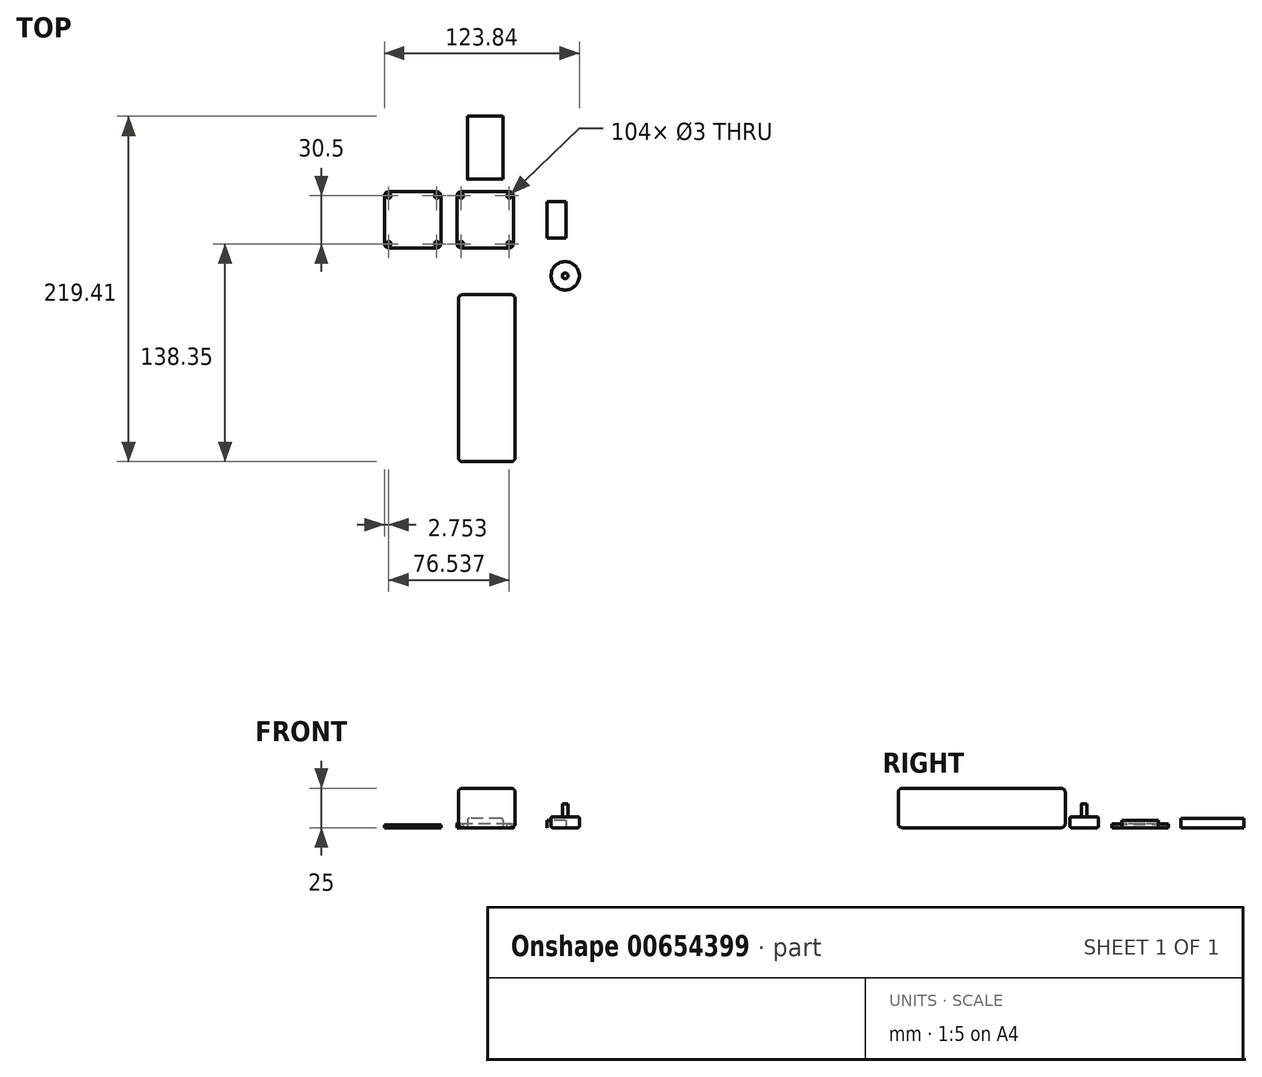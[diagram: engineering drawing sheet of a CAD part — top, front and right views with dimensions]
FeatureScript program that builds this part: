
annotation { "Feature Type Name" : "Feature", "Feature Type Description" : "" }
export const myFeature = defineFeature(function(context is Context, id is Id, definition is map)
    precondition{}
    {
        {
            var Q0;
            Q0=qCreatedBy(makeId("Top.planeOp"),FACE);
            var sketch = newSketch(context, id + "F0", { "sketchPlane" : qUnion([Q0])});
            skLineSegment(sketch, "E0.bottom", {"start": v(18, 18) * mm, "end": v(-18, 18) * mm});
            skLineSegment(sketch, "E0.top", {"start": v(18, -18) * mm, "end": v(-18, -18) * mm});
            skLineSegment(sketch, "E0.left", {"start": v(18, 18) * mm, "end": v(18, -18) * mm});
            skLineSegment(sketch, "E0.right", {"start": v(-18, 18) * mm, "end": v(-18, -18) * mm});
            skPoint(sketch, "E0.middle", {"position": v(0, 0) * mm});
            skSolve(sketch);
        }
        {
            var Q0;
            Q0=qSketchRegion(id+"F0",true);
            extrude(context, id + "F1", {"entities" : qUnion([Q0]), "depth" : 2.54 * mm, "offsetDistance" : 25.4 * mm});
        }
        {
            var Q0;
            Q0=makeQuery(id+"F1.opExtrude","SWEPT_EDGE",EDGE,{"disambiguationData":[OSD([sQuery(id+"F0.wireOp",EDGE,"E0.bottom"),sQuery(id+"F0.wireOp",EDGE,"E0.right")])]});
            var Q1;
            Q1=makeQuery(id+"F1.opExtrude","SWEPT_EDGE",EDGE,{"disambiguationData":[OSD([sQuery(id+"F0.wireOp",EDGE,"E0.bottom"),sQuery(id+"F0.wireOp",EDGE,"E0.left")])]});
            var Q2;
            Q2=makeQuery(id+"F1.opExtrude","SWEPT_EDGE",EDGE,{"disambiguationData":[OSD([sQuery(id+"F0.wireOp",EDGE,"E0.top"),sQuery(id+"F0.wireOp",EDGE,"E0.left")])]});
            var Q3;
            Q3=makeQuery(id+"F1.opExtrude","SWEPT_EDGE",EDGE,{"disambiguationData":[OSD([sQuery(id+"F0.wireOp",EDGE,"E0.top"),sQuery(id+"F0.wireOp",EDGE,"E0.right")])]});
            fillet(context, id + "F2", {"entities" : qUnion([Q0, Q1, Q2, Q3]), "radius" : 3.17 * mm, "tangentPropagation" : true, "allowEdgeOverflow" : false});
        }
        {
            var Q0;
            Q0=makeQuery(id+"F1.opExtrude","CAP_FACE",FACE,{"disambiguationData":[OSD([sQuery(id+"F0.wireOp",EDGE,"E0.bottom"),sQuery(id+"F0.wireOp",EDGE,"E0.top"),sQuery(id+"F0.wireOp",EDGE,"E0.left"),sQuery(id+"F0.wireOp",EDGE,"E0.right")])],"isStart":false});
            var sketch = newSketch(context, id + "F3", { "sketchPlane" : qUnion([Q0])});
            skLineSegment(sketch, "E1.bottom", {"start": v(15.25, 15.25) * mm, "end": v(-15.25, 15.25) * mm, "construction": true});
            skLineSegment(sketch, "E1.top", {"start": v(15.25, -15.25) * mm, "end": v(-15.25, -15.25) * mm, "construction": true});
            skLineSegment(sketch, "E1.left", {"start": v(15.25, 15.25) * mm, "end": v(15.25, -15.25) * mm, "construction": true});
            skLineSegment(sketch, "E1.right", {"start": v(-15.25, 15.25) * mm, "end": v(-15.25, -15.25) * mm, "construction": true});
            skPoint(sketch, "E1.middle", {"position": v(0, 0) * mm});
            skCircle(sketch, "E2", {"center": v(-15.25, 15.25) * mm, "radius": 1.5 * mm});
            skLineSegment(sketch, "E3", {"start": v(-18, 0) * mm, "end": v(18, 0) * mm, "construction": true});
            skLineSegment(sketch, "E4", {"start": v(0, 18) * mm, "end": v(0, -18) * mm, "construction": true});
            skCircle(sketch, "E5.MirrorC", {"center": v(15.25, 15.25) * mm, "radius": 1.5 * mm});
            skCircle(sketch, "E6.MirrorC", {"center": v(-15.25, -15.25) * mm, "radius": 1.5 * mm});
            skCircle(sketch, "E7.MirrorC", {"center": v(15.25, -15.25) * mm, "radius": 1.5 * mm});
            skSolve(sketch);
        }
        {
            var Q0;
            Q0=qSketchRegion(id+"F3",true);
            extrude(context, id + "F4", {"entities" : qUnion([Q0]), "operationType" : NewBodyOperationType.REMOVE, "oppositeDirection" : true, "depth" : 2.54 * mm, "offsetDistance" : 25.4 * mm});
        }
        {
            var Q0;
            Q0=qCreatedBy(makeId("Top.planeOp"),FACE);
            var sketch = newSketch(context, id + "F5", { "sketchPlane" : qUnion([Q0])});
            skLineSegment(sketch, "E8.bottom", {"start": v(51.23, 11.5) * mm, "end": v(39.23, 11.5) * mm});
            skLineSegment(sketch, "E8.top", {"start": v(51.23, -11.5) * mm, "end": v(39.23, -11.5) * mm});
            skLineSegment(sketch, "E8.left", {"start": v(51.23, 11.5) * mm, "end": v(51.23, -11.5) * mm});
            skLineSegment(sketch, "E8.right", {"start": v(39.23, 11.5) * mm, "end": v(39.23, -11.5) * mm});
            skPoint(sketch, "E8.middle", {"position": v(45.23, 0) * mm});
            skSolve(sketch);
        }
        {
            var Q0;
            Q0=qSketchRegion(id+"F5",true);
            extrude(context, id + "F6", {"entities" : qUnion([Q0]), "depth" : 4.5 * mm, "offsetDistance" : 25.4 * mm});
        }
        {
            var Q0;
            Q0=qCreatedBy(makeId("Top.planeOp"),FACE);
            var sketch = newSketch(context, id + "F7", { "sketchPlane" : qUnion([Q0])});
            skLineSegment(sketch, "E9.bottom", {"start": v(-28.04, 18) * mm, "end": v(-64.04, 18) * mm});
            skLineSegment(sketch, "E9.top", {"start": v(-28.04, -18) * mm, "end": v(-64.04, -18) * mm});
            skLineSegment(sketch, "E9.left", {"start": v(-28.04, 18) * mm, "end": v(-28.04, -18) * mm});
            skLineSegment(sketch, "E9.right", {"start": v(-64.04, 18) * mm, "end": v(-64.04, -18) * mm});
            skPoint(sketch, "E9.middle", {"position": v(-46.04, 0) * mm});
            skSolve(sketch);
        }
        {
            var Q0;
            Q0=qSketchRegion(id+"F7",true);
            extrude(context, id + "F8", {"entities" : qUnion([Q0]), "depth" : 1.75 * mm, "offsetDistance" : 25.4 * mm});
        }
        {
            var Q0;
            Q0=makeQuery(id+"F8.opExtrude","CAP_FACE",FACE,{"disambiguationData":[OSD([sQuery(id+"F7.wireOp",EDGE,"E9.bottom"),sQuery(id+"F7.wireOp",EDGE,"E9.top"),sQuery(id+"F7.wireOp",EDGE,"E9.left"),sQuery(id+"F7.wireOp",EDGE,"E9.right")])],"isStart":false});
            var sketch = newSketch(context, id + "F9", { "sketchPlane" : qUnion([Q0])});
            skLineSegment(sketch, "E10", {"start": v(-46.04, 18) * mm, "end": v(-46.04, -18) * mm, "construction": true});
            skLineSegment(sketch, "E11", {"start": v(-64.04, 0) * mm, "end": v(-28.04, 0) * mm, "construction": true});
            skLineSegment(sketch, "E12.bottom", {"start": v(-30.79, 15.25) * mm, "end": v(-61.29, 15.25) * mm, "construction": true});
            skLineSegment(sketch, "E12.top", {"start": v(-30.79, -15.25) * mm, "end": v(-61.29, -15.25) * mm, "construction": true});
            skLineSegment(sketch, "E12.left", {"start": v(-30.79, 15.25) * mm, "end": v(-30.79, -15.25) * mm, "construction": true});
            skLineSegment(sketch, "E12.right", {"start": v(-61.29, 15.25) * mm, "end": v(-61.29, -15.25) * mm, "construction": true});
            skPoint(sketch, "E12.middle", {"position": v(-46.04, 0) * mm});
            skCircle(sketch, "E13", {"center": v(-61.29, 15.25) * mm, "radius": 1.5 * mm});
            skCircle(sketch, "E14.MirrorC", {"center": v(-30.79, 15.25) * mm, "radius": 1.5 * mm});
            skCircle(sketch, "E15.MirrorC", {"center": v(-61.29, -15.25) * mm, "radius": 1.5 * mm});
            skCircle(sketch, "E16.MirrorC", {"center": v(-30.79, -15.25) * mm, "radius": 1.5 * mm});
            skSolve(sketch);
        }
        {
            var Q0;
            Q0=qSketchRegion(id+"F9",true);
            extrude(context, id + "F10", {"entities" : qUnion([Q0]), "operationType" : NewBodyOperationType.REMOVE, "oppositeDirection" : true, "depth" : 1.75 * mm, "offsetDistance" : 25.4 * mm});
        }
        {
            var Q0;
            Q0=makeQuery(id+"F8.opExtrude","SWEPT_EDGE",EDGE,{"disambiguationData":[OSD([sQuery(id+"F7.wireOp",EDGE,"E9.bottom"),sQuery(id+"F7.wireOp",EDGE,"E9.right")])]});
            var Q1;
            Q1=makeQuery(id+"F8.opExtrude","SWEPT_EDGE",EDGE,{"disambiguationData":[OSD([sQuery(id+"F7.wireOp",EDGE,"E9.bottom"),sQuery(id+"F7.wireOp",EDGE,"E9.left")])]});
            var Q2;
            Q2=makeQuery(id+"F8.opExtrude","SWEPT_EDGE",EDGE,{"disambiguationData":[OSD([sQuery(id+"F7.wireOp",EDGE,"E9.top"),sQuery(id+"F7.wireOp",EDGE,"E9.left")])]});
            var Q3;
            Q3=makeQuery(id+"F8.opExtrude","SWEPT_EDGE",EDGE,{"disambiguationData":[OSD([sQuery(id+"F7.wireOp",EDGE,"E9.top"),sQuery(id+"F7.wireOp",EDGE,"E9.right")])]});
            fillet(context, id + "F11", {"entities" : qUnion([Q0, Q1, Q2, Q3]), "radius" : 3.17 * mm, "tangentPropagation" : true, "allowEdgeOverflow" : false});
        }
        {
            var Q0;
            Q0=qCreatedBy(makeId("Top.planeOp"),FACE);
            var sketch = newSketch(context, id + "F12", { "sketchPlane" : qUnion([Q0])});
            skLineSegment(sketch, "E17.bottom", {"start": v(11.25, 65.81) * mm, "end": v(11.25, 25.81) * mm});
            skLineSegment(sketch, "E17.top", {"start": v(-11.25, 65.81) * mm, "end": v(-11.25, 25.81) * mm});
            skLineSegment(sketch, "E17.left", {"start": v(11.25, 65.81) * mm, "end": v(-11.25, 65.81) * mm});
            skLineSegment(sketch, "E17.right", {"start": v(11.25, 25.81) * mm, "end": v(-11.25, 25.81) * mm});
            skPoint(sketch, "E17.middle", {"position": v(0, 45.81) * mm});
            skSolve(sketch);
        }
        {
            var Q0;
            Q0=qSketchRegion(id+"F12",true);
            extrude(context, id + "F13", {"entities" : qUnion([Q0]), "depth" : 6 * mm, "offsetDistance" : 25.4 * mm});
        }
        {
            var Q0;
            Q0=makeQuery(id+"F13.opExtrude","CAP_EDGE",EDGE,{"disambiguationData":[OSD([sQuery(id+"F12.wireOp",EDGE,"E17.bottom")])],"isStart":false});
            var Q1;
            Q1=makeQuery(id+"F13.opExtrude","CAP_EDGE",EDGE,{"disambiguationData":[OSD([sQuery(id+"F12.wireOp",EDGE,"E17.bottom")])],"isStart":true});
            var Q2;
            Q2=makeQuery(id+"F13.opExtrude","CAP_EDGE",EDGE,{"disambiguationData":[OSD([sQuery(id+"F12.wireOp",EDGE,"E17.top")])],"isStart":true});
            var Q3;
            Q3=makeQuery(id+"F13.opExtrude","CAP_EDGE",EDGE,{"disambiguationData":[OSD([sQuery(id+"F12.wireOp",EDGE,"E17.top")])],"isStart":false});
            fillet(context, id + "F14", {"entities" : qUnion([Q0, Q1, Q2, Q3]), "radius" : 1.27 * mm, "tangentPropagation" : true, "allowEdgeOverflow" : false});
        }
        {
            var Q0;
            Q0=qCreatedBy(makeId("Top.planeOp"),FACE);
            var sketch = newSketch(context, id + "F15", { "sketchPlane" : qUnion([Q0])});
            skLineSegment(sketch, "E18.bottom", {"start": v(-17, -47.6) * mm, "end": v(-17, -153.6) * mm});
            skLineSegment(sketch, "E18.top", {"start": v(19, -47.6) * mm, "end": v(19, -153.6) * mm});
            skLineSegment(sketch, "E18.left", {"start": v(-17, -47.6) * mm, "end": v(19, -47.6) * mm});
            skLineSegment(sketch, "E18.right", {"start": v(-17, -153.6) * mm, "end": v(19, -153.6) * mm});
            skPoint(sketch, "E18.middle", {"position": v(1, -100.6) * mm});
            skLineSegment(sketch, "E19", {"start": v(0, 0) * mm, "end": v(0, -101.6) * mm, "construction": true});
            skSolve(sketch);
        }
        {
            var Q0;
            Q0=qSketchRegion(id+"F15",true);
            extrude(context, id + "F16", {"entities" : qUnion([Q0]), "depth" : 25 * mm, "offsetDistance" : 25.4 * mm});
        }
        {
            var Q0;
            Q0=makeQuery(id+"F16.opExtrude","CAP_FACE",FACE,{"disambiguationData":[OSD([sQuery(id+"F15.wireOp",EDGE,"E18.bottom"),sQuery(id+"F15.wireOp",EDGE,"E18.top"),sQuery(id+"F15.wireOp",EDGE,"E18.left"),sQuery(id+"F15.wireOp",EDGE,"E18.right")])],"isStart":false});
            var Q1;
            Q1=makeQuery(id+"F16.opExtrude","SWEPT_FACE",FACE,{"disambiguationData":[OSD([sQuery(id+"F15.wireOp",EDGE,"E18.right")])]});
            var Q2;
            Q2=makeQuery(id+"F16.opExtrude","CAP_FACE",FACE,{"disambiguationData":[OSD([sQuery(id+"F15.wireOp",EDGE,"E18.bottom"),sQuery(id+"F15.wireOp",EDGE,"E18.top"),sQuery(id+"F15.wireOp",EDGE,"E18.left"),sQuery(id+"F15.wireOp",EDGE,"E18.right")])],"isStart":true});
            var Q3;
            Q3=makeQuery(id+"F16.opExtrude","SWEPT_FACE",FACE,{"disambiguationData":[OSD([sQuery(id+"F15.wireOp",EDGE,"E18.left")])]});
            fillet(context, id + "F17", {"entities" : qUnion([Q0, Q1, Q2, Q3]), "radius" : 2.54 * mm, "tangentPropagation" : true, "allowEdgeOverflow" : false});
        }
        {
            var Q0;
            Q0=qCreatedBy(makeId("Top.planeOp"),FACE);
            var sketch = newSketch(context, id + "F18", { "sketchPlane" : qUnion([Q0])});
            skLineSegment(sketch, "E20", {"start": v(0, 0) * mm, "end": v(0, -35.56) * mm, "construction": true});
            skLineSegment(sketch, "E21", {"start": v(0, -35.56) * mm, "end": v(50.8, -35.56) * mm, "construction": true});
            skCircle(sketch, "E22", {"center": v(50.8, -35.56) * mm, "radius": 9 * mm});
            skSolve(sketch);
        }
        {
            var Q0;
            Q0=qSketchRegion(id+"F18",true);
            extrude(context, id + "F19", {"entities" : qUnion([Q0]), "depth" : 7 * mm, "offsetDistance" : 25.4 * mm});
        }
        {
            var Q0;
            Q0=makeQuery(id+"F19.opExtrude","CAP_FACE",FACE,{"disambiguationData":[OSD([sQuery(id+"F18.wireOp",EDGE,"E22")])],"isStart":false});
            var sketch = newSketch(context, id + "F20", { "sketchPlane" : qUnion([Q0])});
            skCircle(sketch, "E23", {"center": v(50.8, -35.56) * mm, "radius": 1.84 * mm});
            skSolve(sketch);
        }
        {
            var Q0;
            Q0=qSketchRegion(id+"F20",true);
            extrude(context, id + "F21", {"entities" : qUnion([Q0]), "operationType" : NewBodyOperationType.ADD, "depth" : 8 * mm, "offsetDistance" : 25.4 * mm});
        }
        {
            var Q0;
            Q0=makeQuery(id+"F19.opExtrude","CAP_FACE",FACE,{"disambiguationData":[OSD([sQuery(id+"F18.wireOp",EDGE,"E22")])],"isStart":true});
            var Q1;
            Q1=makeQuery(id+"F19.opExtrude","CAP_FACE",FACE,{"disambiguationData":[OSD([sQuery(id+"F18.wireOp",EDGE,"E22")])],"isStart":false});
            fillet(context, id + "F22", {"entities" : qUnion([Q0, Q1]), "radius" : 1 * mm, "tangentPropagation" : true, "allowEdgeOverflow" : false});
        }
    });
